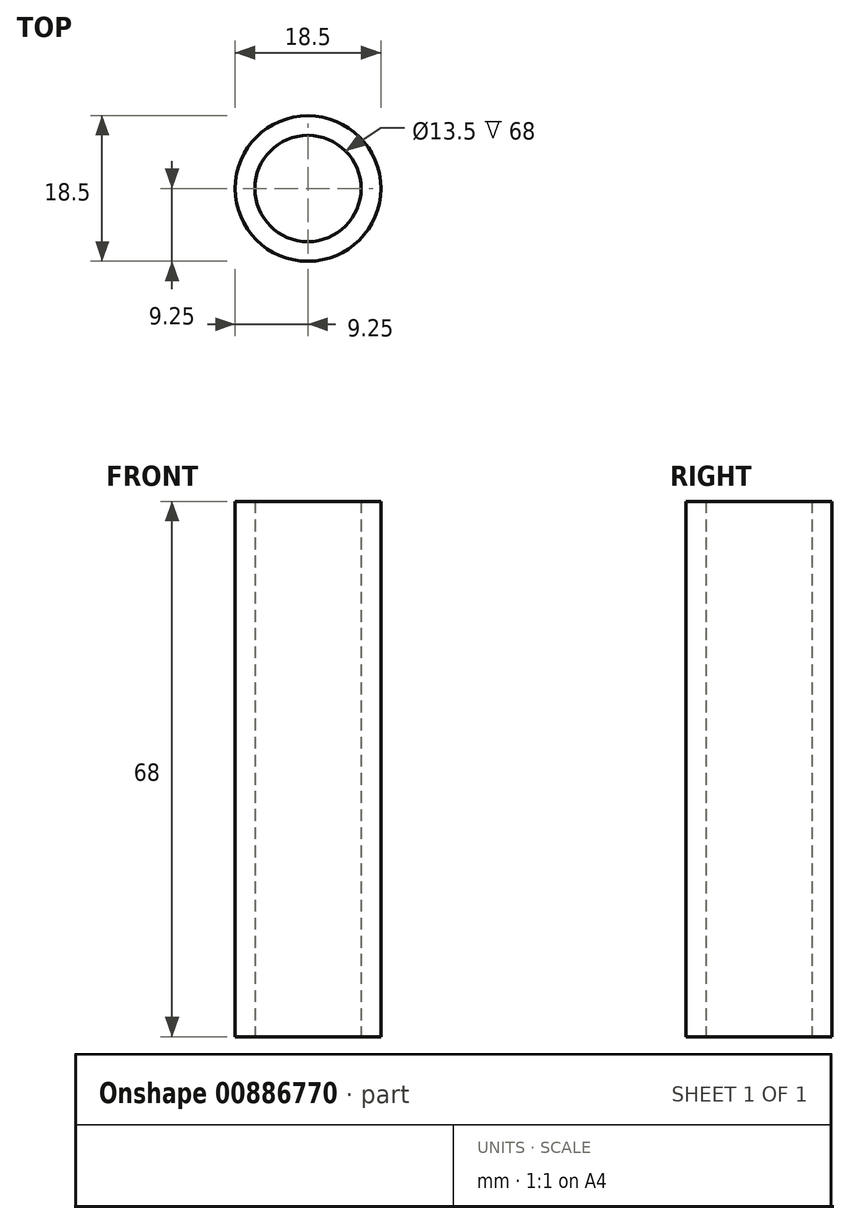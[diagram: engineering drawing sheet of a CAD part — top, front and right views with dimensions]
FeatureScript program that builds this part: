
annotation { "Feature Type Name" : "Feature", "Feature Type Description" : "" }
export const myFeature = defineFeature(function(context is Context, id is Id, definition is map)
    precondition{}
    {
        {
            var Q0;
            Q0=qCreatedBy(makeId("Top.planeOp"),FACE);
            var sketch = newSketch(context, id + "F0", { "sketchPlane" : qUnion([Q0])});
            skCircle(sketch, "E0", {"center": v(0, 0) * mm, "radius": 6.75 * mm});
            skCircle(sketch, "E1.0", {"center": v(0, 0) * mm, "radius": 9.25 * mm});
            skSolve(sketch);
        }
        {
            var Q0;
            Q0=makeQuery(id+"F0.imprint","IMPRINT",FACE,{"disambiguationData":[TD([[makeQuery(id+"F0.imprint","IMPRINT",EDGE,{"derivedFrom":sQuery(id+"F0.wireOp",EDGE,"E0")}),-1.0]])]});
            extrude(context, id + "F1", {"entities" : qUnion([Q0]), "depth" : 68 * mm, "offsetDistance" : 25 * mm});
        }
    });
